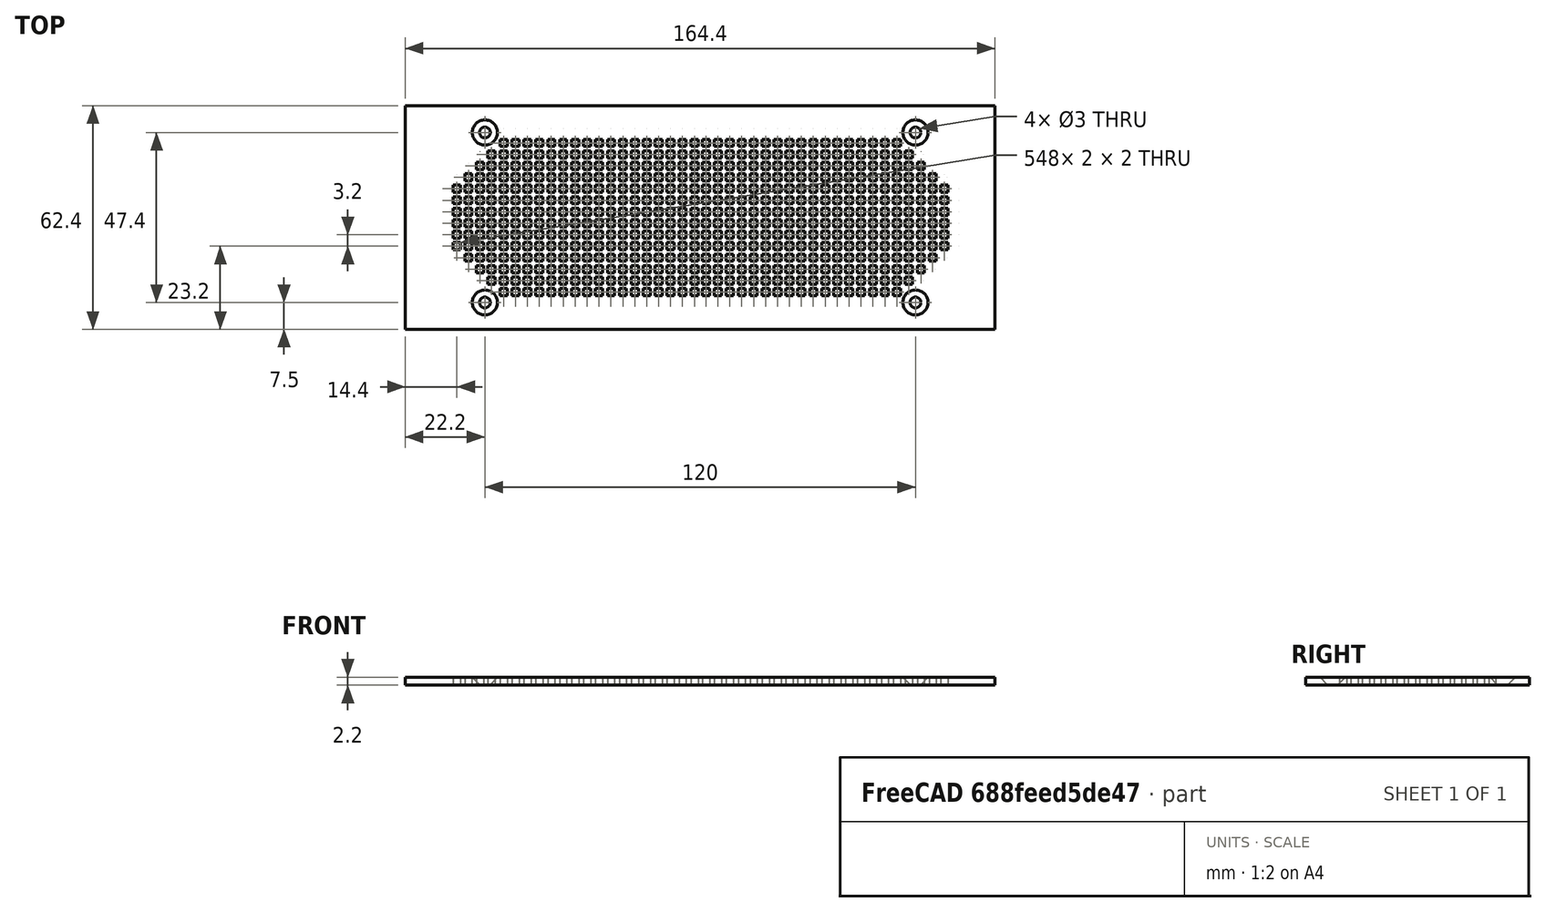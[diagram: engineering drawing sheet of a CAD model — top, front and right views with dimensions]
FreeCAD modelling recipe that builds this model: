
FCSTD DOCUMENT  (FreeCAD 0.19R24276 (Git))
Label: SpeakerCover
License: All rights reserved
LicenseURL: http://en.wikipedia.org/wiki/All_rights_reserved
objects: Sketcher::SketchObject×9, PartDesign::Pocket×8, PartDesign::LinearPattern×7, PartDesign::Pad×1, PartDesign::Chamfer×1, PartDesign::Body×1
note: 37 computed .brp shape members not serialized (recipe doc carries the construction recipe); baked Part::Feature solids carry a one-line shape summary decoded from their .brp

FEATURE [Sketcher::SketchObject] Sketch
  FullyConstrained = true
  MapMode = 5
  Support = -> [XY_Plane]
  sketch-geometry (4):
    g0: LineSegment StartX=-82.2 StartY=31.2 StartZ=0 EndX=82.2 EndY=31.2 EndZ=0
    g1: LineSegment StartX=82.2 StartY=31.2 StartZ=0 EndX=82.2 EndY=-31.2 EndZ=0
    g2: LineSegment StartX=82.2 StartY=-31.2 StartZ=0 EndX=-82.2 EndY=-31.2 EndZ=0
    g3: LineSegment StartX=-82.2 StartY=-31.2 StartZ=0 EndX=-82.2 EndY=31.2 EndZ=0
  constraints (11):
    c: Coincident(g0,g1)
    c: Coincident(g1,g2)
    c: Coincident(g2,g3)
    c: Coincident(g3,g0)
    c: Horizontal(g0)
    c: Horizontal(g2)
    c: Vertical(g1)
    c: Vertical(g3)
    c: Distance(g0) = 164.4
    c: Distance(g3) = 62.4
    c: Symmetric(g0,g1,g-1)
FEATURE [PartDesign::Pad] Pad
  Direction = (1,1,1)
  Length = 2.2
  Length2 = 100
  Profile = -> Sketch
  Type = 0
FEATURE [Sketcher::SketchObject] Sketch001
  FullyConstrained = true
  MapMode = 5
  Placement = pos=(0,0,2.2) rot=(0,0,1;0rad)
  Support = -> [Pad]
  sketch-geometry (4):
    g0: Circle CenterX=-60 CenterY=23.7 CenterZ=0 NormalX=0 NormalY=0 NormalZ=1 AngleXU=0 Radius=1.5
    g1: Circle CenterX=60 CenterY=23.7 CenterZ=0 NormalX=0 NormalY=0 NormalZ=1 AngleXU=0 Radius=1.5
    g2: Circle CenterX=-60 CenterY=-23.7 CenterZ=0 NormalX=0 NormalY=0 NormalZ=1 AngleXU=0 Radius=1.5
    g3: Circle CenterX=60 CenterY=-23.7 CenterZ=0 NormalX=0 NormalY=0 NormalZ=1 AngleXU=0 Radius=1.5
  constraints (12):
    c: DistanceX(g0,g1) = 120
    c: DistanceX(g2,g3) = 120
    c: DistanceY(g2,g0) = 47.4
    c: DistanceY(g3,g1) = 47.4
    c: DistanceY(g-1,g0) = 23.7
    c: DistanceY(g3,g-1) = 23.7
    c: DistanceX(g2,g-1) = 60
    c: DistanceX(g0,g-1) = 60
    c: Radius(g0) = 1.5
    c: Radius(g2) = 1.5
    c: Radius(g3) = 1.5
    c: Radius(g1) = 1.5
FEATURE [PartDesign::Pocket] Pocket
  BaseFeature = -> Pad
  Length = 2.2
  Length2 = 100
  Profile = -> Sketch001
  Type = 0
FEATURE [Sketcher::SketchObject] Sketch002
  FullyConstrained = true
  MapMode = 5
  Placement = pos=(0,0,2.2) rot=(0,0,1;0rad)
  Support = -> [Pocket]
  sketch-geometry (28):
    g0: LineSegment StartX=-2.6 StartY=2.6 StartZ=0 EndX=-0.6 EndY=2.6 EndZ=0
    g1: LineSegment StartX=-0.6 StartY=2.6 StartZ=0 EndX=-0.6 EndY=0.6 EndZ=0
    g2: LineSegment StartX=-0.6 StartY=0.6 StartZ=0 EndX=-2.6 EndY=0.6 EndZ=0
    g3: LineSegment StartX=-2.6 StartY=0.6 StartZ=0 EndX=-2.6 EndY=2.6 EndZ=0
    g4: LineSegment StartX=-2.6 StartY=5.8 StartZ=0 EndX=-0.6 EndY=5.8 EndZ=0
    g5: LineSegment StartX=-0.6 StartY=5.8 StartZ=0 EndX=-0.6 EndY=3.8 EndZ=0
    g6: LineSegment StartX=-0.6 StartY=3.8 StartZ=0 EndX=-2.6 EndY=3.8 EndZ=0
    g7: LineSegment StartX=-2.6 StartY=3.8 StartZ=0 EndX=-2.6 EndY=5.8 EndZ=0
    g8: LineSegment StartX=-2.6 StartY=9 StartZ=0 EndX=-0.6 EndY=9 EndZ=0
    g9: LineSegment StartX=-0.6 StartY=9 StartZ=0 EndX=-0.6 EndY=7 EndZ=0
    g10: LineSegment StartX=-0.6 StartY=7 StartZ=0 EndX=-2.6 EndY=7 EndZ=0
    g11: LineSegment StartX=-2.6 StartY=7 StartZ=0 EndX=-2.6 EndY=9 EndZ=0
    g12: LineSegment StartX=-2.6 StartY=12.2 StartZ=0 EndX=-0.6 EndY=12.2 EndZ=0
    g13: LineSegment StartX=-0.6 StartY=12.2 StartZ=0 EndX=-0.6 EndY=10.2 EndZ=0
    g14: LineSegment StartX=-0.6 StartY=10.2 StartZ=0 EndX=-2.6 EndY=10.2 EndZ=0
    g15: LineSegment StartX=-2.6 StartY=10.2 StartZ=0 EndX=-2.6 EndY=12.2 EndZ=0
    g16: LineSegment StartX=-2.6 StartY=15.4 StartZ=0 EndX=-0.6 EndY=15.4 EndZ=0
    g17: LineSegment StartX=-0.6 StartY=15.4 StartZ=0 EndX=-0.6 EndY=13.4 EndZ=0
    g18: LineSegment StartX=-0.6 StartY=13.4 StartZ=0 EndX=-2.6 EndY=13.4 EndZ=0
    g19: LineSegment StartX=-2.6 StartY=13.4 StartZ=0 EndX=-2.6 EndY=15.4 EndZ=0
    g20: LineSegment StartX=-2.6 StartY=18.6 StartZ=0 EndX=-0.6 EndY=18.6 EndZ=0
    g21: LineSegment StartX=-0.6 StartY=18.6 StartZ=0 EndX=-0.6 EndY=16.6 EndZ=0
    g22: LineSegment StartX=-0.6 StartY=16.6 StartZ=0 EndX=-2.6 EndY=16.6 EndZ=0
    g23: LineSegment StartX=-2.6 StartY=16.6 StartZ=0 EndX=-2.6 EndY=18.6 EndZ=0
    g24: LineSegment StartX=-2.6 StartY=21.8 StartZ=0 EndX=-0.6 EndY=21.8 EndZ=0
    g25: LineSegment StartX=-0.6 StartY=21.8 StartZ=0 EndX=-0.6 EndY=19.8 EndZ=0
    g26: LineSegment StartX=-0.6 StartY=19.8 StartZ=0 EndX=-2.6 EndY=19.8 EndZ=0
    g27: LineSegment StartX=-2.6 StartY=19.8 StartZ=0 EndX=-2.6 EndY=21.8 EndZ=0
  constraints (84):
    c: Coincident(g0,g1)
    c: Coincident(g1,g2)
    c: Coincident(g2,g3)
    c: Coincident(g3,g0)
    c: Horizontal(g0)
    c: Horizontal(g2)
    c: Vertical(g1)
    c: Vertical(g3)
    c: Distance(g0) = 2
    c: Distance(g1) = 2
    c: DistanceX(g1,g-1) = 0.6
    c: DistanceY(g-1,g1) = 0.6
    c: Coincident(g4,g5)
    c: Coincident(g5,g6)
    c: Coincident(g6,g7)
    c: Coincident(g7,g4)
    c: Horizontal(g4)
    c: Horizontal(g6)
    c: Vertical(g5)
    c: Vertical(g7)
    c: Distance(g4) = 2
    c: Distance(g5) = 2
    c: DistanceX(g5,g-1) = 0.6
    c: DistanceY(g0,g5) = 1.2
    c: Coincident(g8,g9)
    c: Coincident(g9,g10)
    c: Coincident(g10,g11)
    c: Coincident(g11,g8)
    c: Horizontal(g8)
    c: Horizontal(g10)
    c: Vertical(g9)
    c: Vertical(g11)
    c: Distance(g8) = 2
    c: Distance(g9) = 2
    c: DistanceX(g9,g-1) = 0.6
    c: DistanceY(g4,g9) = 1.2
    c: Coincident(g12,g13)
    c: Coincident(g13,g14)
    c: Coincident(g14,g15)
    c: Coincident(g15,g12)
    c: Horizontal(g12)
    c: Horizontal(g14)
    c: Vertical(g13)
    c: Vertical(g15)
    c: Distance(g12) = 2
    c: Distance(g13) = 2
    c: DistanceX(g13,g-1) = 0.6
    c: DistanceY(g8,g13) = 1.2
    c: Coincident(g16,g17)
    c: Coincident(g17,g18)
    c: Coincident(g18,g19)
    c: Coincident(g19,g16)
    c: Horizontal(g16)
    c: Horizontal(g18)
    c: Vertical(g17)
    c: Vertical(g19)
    c: Distance(g16) = 2
    c: Distance(g17) = 2
    c: DistanceX(g17,g-1) = 0.6
    c: DistanceY(g12,g17) = 1.2
    c: Coincident(g20,g21)
    c: Coincident(g21,g22)
    c: Coincident(g22,g23)
    c: Coincident(g23,g20)
    c: Horizontal(g20)
    c: Horizontal(g22)
    c: Vertical(g21)
    c: Vertical(g23)
    c: Distance(g20) = 2
    c: Distance(g21) = 2
    c: DistanceY(g16,g21) = 1.2
    c: DistanceX(g21,g-1) = 0.6
    c: Coincident(g24,g25)
    c: Coincident(g25,g26)
    c: Coincident(g26,g27)
    c: Coincident(g27,g24)
    c: Horizontal(g24)
    c: Horizontal(g26)
    c: Vertical(g25)
    c: Vertical(g27)
    c: Distance(g24) = 2
    c: Distance(g25) = 2
    c: DistanceX(g25,g-1) = 0.6
    c: DistanceY(g20,g25) = 1.2
FEATURE [PartDesign::Pocket] Pocket001
  BaseFeature = -> Pocket
  Length = 2.2
  Length2 = 100
  Profile = -> Sketch002
  Type = 0
FEATURE [PartDesign::LinearPattern] LinearPattern
  BaseFeature = -> Pocket001
  Direction = -> Sketch002 [H_Axis]
  Length = 53.2
  Occurrences = 17
  Originals = -> [Pocket001]
  Reversed = true
FEATURE [Sketcher::SketchObject] Sketch003
  FullyConstrained = true
  MapMode = 5
  Placement = pos=(0,0,2.2) rot=(0,0,1;0rad)
  Support = -> [LinearPattern]
  sketch-geometry (28):
    g0: LineSegment StartX=-2.6 StartY=-0.6 StartZ=0 EndX=-0.6 EndY=-0.6 EndZ=0
    g1: LineSegment StartX=-0.6 StartY=-0.6 StartZ=0 EndX=-0.6 EndY=-2.6 EndZ=0
    g2: LineSegment StartX=-0.6 StartY=-2.6 StartZ=0 EndX=-2.6 EndY=-2.6 EndZ=0
    g3: LineSegment StartX=-2.6 StartY=-2.6 StartZ=0 EndX=-2.6 EndY=-0.6 EndZ=0
    g4: LineSegment StartX=-2.6 StartY=-3.8 StartZ=0 EndX=-0.6 EndY=-3.8 EndZ=0
    g5: LineSegment StartX=-0.6 StartY=-3.8 StartZ=0 EndX=-0.6 EndY=-5.8 EndZ=0
    g6: LineSegment StartX=-0.6 StartY=-5.8 StartZ=0 EndX=-2.6 EndY=-5.8 EndZ=0
    g7: LineSegment StartX=-2.6 StartY=-5.8 StartZ=0 EndX=-2.6 EndY=-3.8 EndZ=0
    g8: LineSegment StartX=-2.6 StartY=-7 StartZ=0 EndX=-0.6 EndY=-7 EndZ=0
    g9: LineSegment StartX=-0.6 StartY=-7 StartZ=0 EndX=-0.6 EndY=-9 EndZ=0
    g10: LineSegment StartX=-0.6 StartY=-9 StartZ=0 EndX=-2.6 EndY=-9 EndZ=0
    g11: LineSegment StartX=-2.6 StartY=-9 StartZ=0 EndX=-2.6 EndY=-7 EndZ=0
    g12: LineSegment StartX=-2.6 StartY=-10.2 StartZ=0 EndX=-0.6 EndY=-10.2 EndZ=0
    g13: LineSegment StartX=-0.6 StartY=-10.2 StartZ=0 EndX=-0.6 EndY=-12.2 EndZ=0
    g14: LineSegment StartX=-0.6 StartY=-12.2 StartZ=0 EndX=-2.6 EndY=-12.2 EndZ=0
    g15: LineSegment StartX=-2.6 StartY=-12.2 StartZ=0 EndX=-2.6 EndY=-10.2 EndZ=0
    g16: LineSegment StartX=-2.6 StartY=-13.4 StartZ=0 EndX=-0.6 EndY=-13.4 EndZ=0
    g17: LineSegment StartX=-0.6 StartY=-13.4 StartZ=0 EndX=-0.6 EndY=-15.4 EndZ=0
    g18: LineSegment StartX=-0.6 StartY=-15.4 StartZ=0 EndX=-2.6 EndY=-15.4 EndZ=0
    g19: LineSegment StartX=-2.6 StartY=-15.4 StartZ=0 EndX=-2.6 EndY=-13.4 EndZ=0
    g20: LineSegment StartX=-2.6 StartY=-16.6 StartZ=0 EndX=-0.6 EndY=-16.6 EndZ=0
    g21: LineSegment StartX=-0.6 StartY=-16.6 StartZ=0 EndX=-0.6 EndY=-18.6 EndZ=0
    g22: LineSegment StartX=-0.6 StartY=-18.6 StartZ=0 EndX=-2.6 EndY=-18.6 EndZ=0
    g23: LineSegment StartX=-2.6 StartY=-18.6 StartZ=0 EndX=-2.6 EndY=-16.6 EndZ=0
    g24: LineSegment StartX=-2.6 StartY=-19.8 StartZ=0 EndX=-0.6 EndY=-19.8 EndZ=0
    g25: LineSegment StartX=-0.6 StartY=-19.8 StartZ=0 EndX=-0.6 EndY=-21.8 EndZ=0
    g26: LineSegment StartX=-0.6 StartY=-21.8 StartZ=0 EndX=-2.6 EndY=-21.8 EndZ=0
    g27: LineSegment StartX=-2.6 StartY=-21.8 StartZ=0 EndX=-2.6 EndY=-19.8 EndZ=0
  constraints (84):
    c: Coincident(g0,g1)
    c: Coincident(g1,g2)
    c: Coincident(g2,g3)
    c: Coincident(g3,g0)
    c: Horizontal(g0)
    c: Horizontal(g2)
    c: Vertical(g1)
    c: Vertical(g3)
    c: Coincident(g4,g5)
    c: Coincident(g5,g6)
    c: Coincident(g6,g7)
    c: Coincident(g7,g4)
    c: Horizontal(g4)
    c: Horizontal(g6)
    c: Vertical(g5)
    c: Vertical(g7)
    c: Coincident(g8,g9)
    c: Coincident(g9,g10)
    c: Coincident(g10,g11)
    c: Coincident(g11,g8)
    c: Horizontal(g8)
    c: Horizontal(g10)
    c: Vertical(g9)
    c: Vertical(g11)
    c: Coincident(g12,g13)
    c: Coincident(g13,g14)
    c: Coincident(g14,g15)
    c: Coincident(g15,g12)
    c: Horizontal(g12)
    c: Horizontal(g14)
    c: Vertical(g13)
    c: Vertical(g15)
    c: Coincident(g16,g17)
    c: Coincident(g17,g18)
    c: Coincident(g18,g19)
    c: Coincident(g19,g16)
    c: Horizontal(g16)
    c: Horizontal(g18)
    c: Vertical(g17)
    c: Vertical(g19)
    c: Coincident(g20,g21)
    c: Coincident(g21,g22)
    c: Coincident(g22,g23)
    c: Coincident(g23,g20)
    c: Horizontal(g20)
    c: Horizontal(g22)
    c: Vertical(g21)
    c: Vertical(g23)
    c: Coincident(g24,g25)
    c: Coincident(g25,g26)
    c: Coincident(g26,g27)
    c: Coincident(g27,g24)
    c: Horizontal(g24)
    c: Horizontal(g26)
    c: Vertical(g25)
    c: Vertical(g27)
    c: Distance(g0) = 2
    c: Distance(g1) = 2
    c: Distance(g4) = 2
    c: Distance(g5) = 2
    c: Distance(g8) = 2
    c: Distance(g9) = 2
    c: Distance(g12) = 2
    c: Distance(g13) = 2
    c: Distance(g16) = 2
    c: Distance(g17) = 2
    c: Distance(g20) = 2
    c: Distance(g21) = 2
    c: Distance(g24) = 2
    c: Distance(g25) = 2
    c: DistanceY(g0,g-1) = 0.6
    c: DistanceY(g4,g1) = 1.2
    c: DistanceY(g8,g5) = 1.2
    c: DistanceX(g0,g-1) = 0.6
    c: DistanceX(g4,g-1) = 0.6
    c: DistanceX(g8,g-1) = 0.6
    c: DistanceX(g12,g-1) = 0.6
    c: DistanceX(g16,g-1) = 0.6
    c: DistanceX(g20,g-1) = 0.6
    c: DistanceX(g24,g-1) = 0.6
    c: DistanceY(g12,g9) = 1.2
    c: DistanceY(g16,g13) = 1.2
    c: DistanceY(g20,g17) = 1.2
    c: DistanceY(g24,g21) = 1.2
FEATURE [PartDesign::Pocket] Pocket002
  BaseFeature = -> LinearPattern
  Length = 2.2
  Length2 = 100
  Profile = -> Sketch003
  Type = 0
FEATURE [PartDesign::LinearPattern] LinearPattern001
  BaseFeature = -> Pocket002
  Direction = -> Sketch003 [H_Axis]
  Length = 53.2
  Occurrences = 17
  Originals = -> [Pocket002]
  Reversed = true
FEATURE [Sketcher::SketchObject] Sketch004
  FullyConstrained = true
  MapMode = 5
  Placement = pos=(0,0,2.2) rot=(0,0,1;0rad)
  Support = -> [LinearPattern001]
  sketch-geometry (56):
    g0: LineSegment StartX=0.6 StartY=2.6 StartZ=0 EndX=2.6 EndY=2.6 EndZ=0
    g1: LineSegment StartX=2.6 StartY=2.6 StartZ=0 EndX=2.6 EndY=0.6 EndZ=0
    g2: LineSegment StartX=2.6 StartY=0.6 StartZ=0 EndX=0.6 EndY=0.6 EndZ=0
    g3: LineSegment StartX=0.6 StartY=0.6 StartZ=0 EndX=0.6 EndY=2.6 EndZ=0
    g4: LineSegment StartX=0.6 StartY=5.8 StartZ=0 EndX=2.6 EndY=5.8 EndZ=0
    g5: LineSegment StartX=2.6 StartY=5.8 StartZ=0 EndX=2.6 EndY=3.8 EndZ=0
    g6: LineSegment StartX=2.6 StartY=3.8 StartZ=0 EndX=0.6 EndY=3.8 EndZ=0
    g7: LineSegment StartX=0.6 StartY=3.8 StartZ=0 EndX=0.6 EndY=5.8 EndZ=0
    g8: LineSegment StartX=0.6 StartY=9 StartZ=0 EndX=2.6 EndY=9 EndZ=0
    g9: LineSegment StartX=2.6 StartY=9 StartZ=0 EndX=2.6 EndY=7 EndZ=0
    g10: LineSegment StartX=2.6 StartY=7 StartZ=0 EndX=0.6 EndY=7 EndZ=0
    g11: LineSegment StartX=0.6 StartY=7 StartZ=0 EndX=0.6 EndY=9 EndZ=0
    g12: LineSegment StartX=0.6 StartY=12.2 StartZ=0 EndX=2.6 EndY=12.2 EndZ=0
    g13: LineSegment StartX=2.6 StartY=12.2 StartZ=0 EndX=2.6 EndY=10.2 EndZ=0
    g14: LineSegment StartX=2.6 StartY=10.2 StartZ=0 EndX=0.6 EndY=10.2 EndZ=0
    g15: LineSegment StartX=0.6 StartY=10.2 StartZ=0 EndX=0.6 EndY=12.2 EndZ=0
    g16: LineSegment StartX=0.6 StartY=15.4 StartZ=0 EndX=2.6 EndY=15.4 EndZ=0
    g17: LineSegment StartX=2.6 StartY=15.4 StartZ=0 EndX=2.6 EndY=13.4 EndZ=0
    g18: LineSegment StartX=2.6 StartY=13.4 StartZ=0 EndX=0.6 EndY=13.4 EndZ=0
    g19: LineSegment StartX=0.6 StartY=13.4 StartZ=0 EndX=0.6 EndY=15.4 EndZ=0
    g20: LineSegment StartX=0.6 StartY=21.8 StartZ=0 EndX=2.6 EndY=21.8 EndZ=0
    g21: LineSegment StartX=2.6 StartY=21.8 StartZ=0 EndX=2.6 EndY=19.8 EndZ=0
    g22: LineSegment StartX=2.6 StartY=19.8 StartZ=0 EndX=0.6 EndY=19.8 EndZ=0
    g23: LineSegment StartX=0.6 StartY=19.8 StartZ=0 EndX=0.6 EndY=21.8 EndZ=0
    g24: LineSegment StartX=0.6 StartY=18.6 StartZ=0 EndX=2.6 EndY=18.6 EndZ=0
    g25: LineSegment StartX=2.6 StartY=18.6 StartZ=0 EndX=2.6 EndY=16.6 EndZ=0
    g26: LineSegment StartX=2.6 StartY=16.6 StartZ=0 EndX=0.6 EndY=16.6 EndZ=0
    g27: LineSegment StartX=0.6 StartY=16.6 StartZ=0 EndX=0.6 EndY=18.6 EndZ=0
    g28: LineSegment StartX=0.6 StartY=-0.6 StartZ=0 EndX=2.6 EndY=-0.6 EndZ=0
    g29: LineSegment StartX=2.6 StartY=-0.6 StartZ=0 EndX=2.6 EndY=-2.6 EndZ=0
    g30: LineSegment StartX=2.6 StartY=-2.6 StartZ=0 EndX=0.6 EndY=-2.6 EndZ=0
    g31: LineSegment StartX=0.6 StartY=-2.6 StartZ=0 EndX=0.6 EndY=-0.6 EndZ=0
    g32: LineSegment StartX=0.6 StartY=-3.8 StartZ=0 EndX=2.6 EndY=-3.8 EndZ=0
    g33: LineSegment StartX=2.6 StartY=-3.8 StartZ=0 EndX=2.6 EndY=-5.8 EndZ=0
    g34: LineSegment StartX=2.6 StartY=-5.8 StartZ=0 EndX=0.6 EndY=-5.8 EndZ=0
    g35: LineSegment StartX=0.6 StartY=-5.8 StartZ=0 EndX=0.6 EndY=-3.8 EndZ=0
    g36: LineSegment StartX=0.6 StartY=-10.2 StartZ=0 EndX=2.6 EndY=-10.2 EndZ=0
    g37: LineSegment StartX=2.6 StartY=-10.2 StartZ=0 EndX=2.6 EndY=-12.2 EndZ=0
    g38: LineSegment StartX=2.6 StartY=-12.2 StartZ=0 EndX=0.6 EndY=-12.2 EndZ=0
    g39: LineSegment StartX=0.6 StartY=-12.2 StartZ=0 EndX=0.6 EndY=-10.2 EndZ=0
    g40: LineSegment StartX=0.6 StartY=-16.6 StartZ=0 EndX=2.6 EndY=-16.6 EndZ=0
    g41: LineSegment StartX=2.6 StartY=-16.6 StartZ=0 EndX=2.6 EndY=-18.6 EndZ=0
    g42: LineSegment StartX=2.6 StartY=-18.6 StartZ=0 EndX=0.6 EndY=-18.6 EndZ=0
    g43: LineSegment StartX=0.6 StartY=-18.6 StartZ=0 EndX=0.6 EndY=-16.6 EndZ=0
    g44: LineSegment StartX=0.6 StartY=-13.4 StartZ=0 EndX=2.6 EndY=-13.4 EndZ=0
    g45: LineSegment StartX=2.6 StartY=-13.4 StartZ=0 EndX=2.6 EndY=-15.4 EndZ=0
    g46: LineSegment StartX=2.6 StartY=-15.4 StartZ=0 EndX=0.6 EndY=-15.4 EndZ=0
    g47: LineSegment StartX=0.6 StartY=-15.4 StartZ=0 EndX=0.6 EndY=-13.4 EndZ=0
    g48: LineSegment StartX=0.6 StartY=-19.8 StartZ=0 EndX=2.6 EndY=-19.8 EndZ=0
    g49: LineSegment StartX=2.6 StartY=-19.8 StartZ=0 EndX=2.6 EndY=-21.8 EndZ=0
    g50: LineSegment StartX=2.6 StartY=-21.8 StartZ=0 EndX=0.6 EndY=-21.8 EndZ=0
    g51: LineSegment StartX=0.6 StartY=-21.8 StartZ=0 EndX=0.6 EndY=-19.8 EndZ=0
    g52: LineSegment StartX=0.6 StartY=-7 StartZ=0 EndX=2.6 EndY=-7 EndZ=0
    g53: LineSegment StartX=2.6 StartY=-7 StartZ=0 EndX=2.6 EndY=-9 EndZ=0
    g54: LineSegment StartX=2.6 StartY=-9 StartZ=0 EndX=0.6 EndY=-9 EndZ=0
    g55: LineSegment StartX=0.6 StartY=-9 StartZ=0 EndX=0.6 EndY=-7 EndZ=0
  constraints (168):
    c: Coincident(g0,g1)
    c: Coincident(g1,g2)
    c: Coincident(g2,g3)
    c: Coincident(g3,g0)
    c: Horizontal(g0)
    c: Horizontal(g2)
    c: Vertical(g1)
    c: Vertical(g3)
    c: Coincident(g4,g5)
    c: Coincident(g5,g6)
    c: Coincident(g6,g7)
    c: Coincident(g7,g4)
    c: Horizontal(g4)
    c: Horizontal(g6)
    c: Vertical(g5)
    c: Vertical(g7)
    c: Coincident(g8,g9)
    c: Coincident(g9,g10)
    c: Coincident(g10,g11)
    c: Coincident(g11,g8)
    c: Horizontal(g8)
    c: Horizontal(g10)
    c: Vertical(g9)
    c: Vertical(g11)
    c: Coincident(g12,g13)
    c: Coincident(g13,g14)
    c: Coincident(g14,g15)
    c: Coincident(g15,g12)
    c: Horizontal(g12)
    c: Horizontal(g14)
    c: Vertical(g13)
    c: Vertical(g15)
    c: Coincident(g16,g17)
    c: Coincident(g17,g18)
    c: Coincident(g18,g19)
    c: Coincident(g19,g16)
    c: Horizontal(g16)
    c: Horizontal(g18)
    c: Vertical(g17)
    c: Vertical(g19)
    c: Coincident(g20,g21)
    c: Coincident(g21,g22)
    c: Coincident(g22,g23)
    c: Coincident(g23,g20)
    c: Horizontal(g20)
    c: Horizontal(g22)
    c: Vertical(g21)
    c: Vertical(g23)
    c: Coincident(g24,g25)
    c: Coincident(g25,g26)
    c: Coincident(g26,g27)
    c: Coincident(g27,g24)
    c: Horizontal(g24)
    c: Horizontal(g26)
    c: Vertical(g25)
    c: Vertical(g27)
    c: Distance(g0) = 2
    c: Distance(g1) = 2
    c: Distance(g4) = 2
    c: Distance(g5) = 2
    c: Distance(g8) = 2
    c: Distance(g9) = 2
    c: Distance(g12) = 2
    c: Distance(g13) = 2
    c: Distance(g16) = 2
    c: Distance(g17) = 2
    c: Distance(g20) = 2
    c: Distance(g23) = 2
    c: Distance(g25) = 2
    c: Distance(g24) = 2
    c: DistanceY(g-1,g2) = 0.6
    c: DistanceY(g0,g6) = 1.2
    c: DistanceY(g4,g10) = 1.2
    c: DistanceY(g8,g14) = 1.2
    c: DistanceX(g-1,g2) = 0.6
    c: DistanceX(g-1,g6) = 0.6
    c: DistanceX(g-1,g10) = 0.6
    c: DistanceX(g-1,g14) = 0.6
    c: DistanceX(g-1,g18) = 0.6
    c: DistanceY(g12,g18) = 1.2
    c: DistanceY(g16,g26) = 1.2
    c: DistanceY(g24,g22) = 1.2
    c: DistanceX(g-1,g26) = 0.6
    c: DistanceX(g-1,g22) = 0.6
    c: Coincident(g28,g29)
    c: Coincident(g29,g30)
    c: Coincident(g30,g31)
    c: Coincident(g31,g28)
    c: Horizontal(g28)
    c: Horizontal(g30)
    c: Vertical(g29)
    c: Vertical(g31)
    c: Coincident(g32,g33)
    c: Coincident(g33,g34)
    c: Coincident(g34,g35)
    c: Coincident(g35,g32)
    c: Horizontal(g32)
    c: Horizontal(g34)
    c: Vertical(g33)
    c: Vertical(g35)
    c: Coincident(g36,g37)
    c: Coincident(g37,g38)
    c: Coincident(g38,g39)
    c: Coincident(g39,g36)
    c: Horizontal(g36)
    c: Horizontal(g38)
    c: Vertical(g37)
    c: Vertical(g39)
    c: Coincident(g40,g41)
    c: Coincident(g41,g42)
    c: Coincident(g42,g43)
    c: Coincident(g43,g40)
    c: Horizontal(g40)
    c: Horizontal(g42)
    c: Vertical(g41)
    c: Vertical(g43)
    c: Coincident(g44,g45)
    c: Coincident(g45,g46)
    c: Coincident(g46,g47)
    c: Coincident(g47,g44)
    c: Horizontal(g44)
    c: Horizontal(g46)
    c: Vertical(g45)
    c: Vertical(g47)
    c: Coincident(g48,g49)
    c: Coincident(g49,g50)
    c: Coincident(g50,g51)
    c: Coincident(g51,g48)
    c: Horizontal(g48)
    c: Horizontal(g50)
    c: Vertical(g49)
    c: Vertical(g51)
    c: Coincident(g52,g53)
    c: Coincident(g53,g54)
    c: Coincident(g54,g55)
    c: Coincident(g55,g52)
    c: Horizontal(g52)
    c: Horizontal(g54)
    c: Vertical(g53)
    c: Vertical(g55)
    c: Distance(g28) = 2
    c: Distance(g29) = 2
    c: Distance(g32) = 2
    c: Distance(g33) = 2
    c: Distance(g52) = 2
    c: Distance(g53) = 2
    c: DistanceY(g28,g-1) = 0.6
    c: DistanceY(g32,g30) = 1.2
    c: DistanceY(g52,g34) = 1.2
    c: DistanceX(g-1,g28) = 0.6
    c: DistanceX(g-1,g32) = 0.6
    c: DistanceX(g-1,g52) = 0.6
    c: Distance(g36) = 2
    c: Distance(g37) = 2
    c: Distance(g46) = 2
    c: Distance(g45) = 2
    c: DistanceX(g-1,g36) = 0.6
    c: DistanceX(g-1,g44) = 0.6
    c: DistanceY(g36,g54) = 1.2
    c: DistanceY(g44,g38) = 1.2
    c: Distance(g40) = 2
    c: Distance(g41) = 2
    c: Distance(g51) = 2
    c: Distance(g48) = 2
    c: DistanceY(g40,g46) = 1.2
    c: DistanceY(g48,g42) = 1.2
    c: DistanceX(g-1,g40) = 0.6
    c: DistanceX(g-1,g48) = 0.6
FEATURE [PartDesign::Pocket] Pocket003
  BaseFeature = -> LinearPattern001
  Length = 2.2
  Length2 = 100
  Profile = -> Sketch004
  Type = 0
FEATURE [PartDesign::LinearPattern] LinearPattern002
  BaseFeature = -> Pocket003
  Direction = -> Sketch004 [H_Axis]
  Length = 53.2
  Occurrences = 17
  Originals = -> [Pocket003]
FEATURE [Sketcher::SketchObject] Sketch005
  FullyConstrained = true
  MapMode = 5
  Placement = pos=(0,0,2.2) rot=(0,0,1;0rad)
  Support = -> [LinearPattern002]
  sketch-geometry (48):
    g0: LineSegment StartX=-59.2 StartY=2.6 StartZ=0 EndX=-57.2 EndY=2.6 EndZ=0
    g1: LineSegment StartX=-57.2 StartY=2.6 StartZ=0 EndX=-57.2 EndY=0.6 EndZ=0
    g2: LineSegment StartX=-57.2 StartY=0.6 StartZ=0 EndX=-59.2 EndY=0.6 EndZ=0
    g3: LineSegment StartX=-59.2 StartY=0.6 StartZ=0 EndX=-59.2 EndY=2.6 EndZ=0
    g4: LineSegment StartX=-59.2 StartY=-0.6 StartZ=0 EndX=-57.2 EndY=-0.6 EndZ=0
    g5: LineSegment StartX=-57.2 StartY=-0.6 StartZ=0 EndX=-57.2 EndY=-2.6 EndZ=0
    g6: LineSegment StartX=-57.2 StartY=-2.6 StartZ=0 EndX=-59.2 EndY=-2.6 EndZ=0
    g7: LineSegment StartX=-59.2 StartY=-2.6 StartZ=0 EndX=-59.2 EndY=-0.6 EndZ=0
    g8: LineSegment StartX=-59.2 StartY=5.8 StartZ=0 EndX=-57.2 EndY=5.8 EndZ=0
    g9: LineSegment StartX=-57.2 StartY=5.8 StartZ=0 EndX=-57.2 EndY=3.8 EndZ=0
    g10: LineSegment StartX=-57.2 StartY=3.8 StartZ=0 EndX=-59.2 EndY=3.8 EndZ=0
    g11: LineSegment StartX=-59.2 StartY=3.8 StartZ=0 EndX=-59.2 EndY=5.8 EndZ=0
    g12: LineSegment StartX=-59.2 StartY=9 StartZ=0 EndX=-57.2 EndY=9 EndZ=0
    g13: LineSegment StartX=-57.2 StartY=9 StartZ=0 EndX=-57.2 EndY=7 EndZ=0
    g14: LineSegment StartX=-57.2 StartY=7 StartZ=0 EndX=-59.2 EndY=7 EndZ=0
    g15: LineSegment StartX=-59.2 StartY=7 StartZ=0 EndX=-59.2 EndY=9 EndZ=0
    g16: LineSegment StartX=-59.2 StartY=12.2 StartZ=0 EndX=-57.2 EndY=12.2 EndZ=0
    g17: LineSegment StartX=-57.2 StartY=12.2 StartZ=0 EndX=-57.2 EndY=10.2 EndZ=0
    g18: LineSegment StartX=-57.2 StartY=10.2 StartZ=0 EndX=-59.2 EndY=10.2 EndZ=0
    g19: LineSegment StartX=-59.2 StartY=10.2 StartZ=0 EndX=-59.2 EndY=12.2 EndZ=0
    g20: LineSegment StartX=-59.2 StartY=15.4 StartZ=0 EndX=-57.2 EndY=15.4 EndZ=0
    g21: LineSegment StartX=-57.2 StartY=15.4 StartZ=0 EndX=-57.2 EndY=13.4 EndZ=0
    g22: LineSegment StartX=-57.2 StartY=13.4 StartZ=0 EndX=-59.2 EndY=13.4 EndZ=0
    g23: LineSegment StartX=-59.2 StartY=13.4 StartZ=0 EndX=-59.2 EndY=15.4 EndZ=0
    g24: LineSegment StartX=-57.2 StartY=18.6 StartZ=0 EndX=-59.2 EndY=18.6 EndZ=0
    g25: LineSegment StartX=-59.2 StartY=18.6 StartZ=0 EndX=-59.2 EndY=16.6 EndZ=0
    g26: LineSegment StartX=-59.2 StartY=16.6 StartZ=0 EndX=-57.2 EndY=16.6 EndZ=0
    g27: LineSegment StartX=-57.2 StartY=16.6 StartZ=0 EndX=-57.2 EndY=18.6 EndZ=0
    g28: LineSegment StartX=-57.2 StartY=-3.8 StartZ=0 EndX=-59.2 EndY=-3.8 EndZ=0
    g29: LineSegment StartX=-59.2 StartY=-3.8 StartZ=0 EndX=-59.2 EndY=-5.8 EndZ=0
    g30: LineSegment StartX=-59.2 StartY=-5.8 StartZ=0 EndX=-57.2 EndY=-5.8 EndZ=0
    g31: LineSegment StartX=-57.2 StartY=-5.8 StartZ=0 EndX=-57.2 EndY=-3.8 EndZ=0
    g32: LineSegment StartX=-57.2 StartY=-7 StartZ=0 EndX=-59.2 EndY=-7 EndZ=0
    g33: LineSegment StartX=-59.2 StartY=-7 StartZ=0 EndX=-59.2 EndY=-9 EndZ=0
    g34: LineSegment StartX=-59.2 StartY=-9 StartZ=0 EndX=-57.2 EndY=-9 EndZ=0
    g35: LineSegment StartX=-57.2 StartY=-9 StartZ=0 EndX=-57.2 EndY=-7 EndZ=0
    g36: LineSegment StartX=-57.2 StartY=-10.2 StartZ=0 EndX=-59.2 EndY=-10.2 EndZ=0
    g37: LineSegment StartX=-59.2 StartY=-10.2 StartZ=0 EndX=-59.2 EndY=-12.2 EndZ=0
    g38: LineSegment StartX=-59.2 StartY=-12.2 StartZ=0 EndX=-57.2 EndY=-12.2 EndZ=0
    g39: LineSegment StartX=-57.2 StartY=-12.2 StartZ=0 EndX=-57.2 EndY=-10.2 EndZ=0
    g40: LineSegment StartX=-59.2 StartY=-13.4 StartZ=0 EndX=-57.2 EndY=-13.4 EndZ=0
    g41: LineSegment StartX=-57.2 StartY=-13.4 StartZ=0 EndX=-57.2 EndY=-15.4 EndZ=0
    g42: LineSegment StartX=-57.2 StartY=-15.4 StartZ=0 EndX=-59.2 EndY=-15.4 EndZ=0
    g43: LineSegment StartX=-59.2 StartY=-15.4 StartZ=0 EndX=-59.2 EndY=-13.4 EndZ=0
    g44: LineSegment StartX=-59.2 StartY=-16.6 StartZ=0 EndX=-57.2 EndY=-16.6 EndZ=0
    g45: LineSegment StartX=-57.2 StartY=-16.6 StartZ=0 EndX=-57.2 EndY=-18.6 EndZ=0
    g46: LineSegment StartX=-57.2 StartY=-18.6 StartZ=0 EndX=-59.2 EndY=-18.6 EndZ=0
    g47: LineSegment StartX=-59.2 StartY=-18.6 StartZ=0 EndX=-59.2 EndY=-16.6 EndZ=0
  constraints (144):
    c: Coincident(g0,g1)
    c: Coincident(g1,g2)
    c: Coincident(g2,g3)
    c: Coincident(g3,g0)
    c: Horizontal(g0)
    c: Horizontal(g2)
    c: Vertical(g1)
    c: Vertical(g3)
    c: Coincident(g4,g5)
    c: Coincident(g5,g6)
    c: Coincident(g6,g7)
    c: Coincident(g7,g4)
    c: Horizontal(g4)
    c: Horizontal(g6)
    c: Vertical(g5)
    c: Vertical(g7)
    c: Distance(g4) = 2
    c: Distance(g5) = 2
    c: Distance(g0) = 2
    c: Distance(g1) = 2
    c: DistanceY(g4,g-1) = 0.6
    c: DistanceY(g-1,g1) = 0.6
    c: DistanceX(g1,g-1) = 57.2
    c: DistanceX(g4,g-1) = 57.2
    c: Coincident(g8,g9)
    c: Coincident(g9,g10)
    c: Coincident(g10,g11)
    c: Coincident(g11,g8)
    c: Horizontal(g8)
    c: Horizontal(g10)
    c: Vertical(g9)
    c: Vertical(g11)
    c: Coincident(g12,g13)
    c: Coincident(g13,g14)
    c: Coincident(g14,g15)
    c: Coincident(g15,g12)
    c: Horizontal(g12)
    c: Horizontal(g14)
    c: Vertical(g13)
    c: Vertical(g15)
    c: Coincident(g16,g17)
    c: Coincident(g17,g18)
    c: Coincident(g18,g19)
    c: Coincident(g19,g16)
    c: Horizontal(g16)
    c: Horizontal(g18)
    c: Vertical(g17)
    c: Vertical(g19)
    c: Coincident(g20,g21)
    c: Coincident(g21,g22)
    c: Coincident(g22,g23)
    c: Coincident(g23,g20)
    c: Horizontal(g20)
    c: Horizontal(g22)
    c: Vertical(g21)
    c: Vertical(g23)
    c: Coincident(g24,g25)
    c: Coincident(g25,g26)
    c: Coincident(g26,g27)
    c: Coincident(g27,g24)
    c: Horizontal(g24)
    c: Horizontal(g26)
    c: Vertical(g25)
    c: Vertical(g27)
    c: Coincident(g28,g29)
    c: Coincident(g29,g30)
    c: Coincident(g30,g31)
    c: Coincident(g31,g28)
    c: Horizontal(g28)
    c: Horizontal(g30)
    c: Vertical(g29)
    c: Vertical(g31)
    c: Coincident(g32,g33)
    c: Coincident(g33,g34)
    c: Coincident(g34,g35)
    c: Coincident(g35,g32)
    c: Horizontal(g32)
    c: Horizontal(g34)
    c: Vertical(g33)
    c: Vertical(g35)
    c: Coincident(g36,g37)
    c: Coincident(g37,g38)
    c: Coincident(g38,g39)
    c: Coincident(g39,g36)
    c: Horizontal(g36)
    c: Horizontal(g38)
    c: Vertical(g37)
    c: Vertical(g39)
    c: Distance(g8) = 2
    c: Distance(g9) = 2
    c: Distance(g13) = 2
    c: Distance(g12) = 2
    c: Distance(g18) = 2
    c: Distance(g19) = 2
    c: Distance(g21) = 2
    c: Distance(g22) = 2
    c: DistanceY(g0,g9) = 1.2
    c: DistanceY(g8,g14) = 1.2
    c: DistanceY(g12,g18) = 1.2
    c: DistanceY(g16,g22) = 1.2
    c: DistanceX(g9,g-1) = 57.2
    c: DistanceX(g13,g-1) = 57.2
    c: DistanceX(g17,g-1) = 57.2
    c: DistanceX(g21,g-1) = 57.2
    c: Distance(g24) = 2
    c: Distance(g27) = 2
    c: DistanceY(g20,g25) = 1.2
    c: DistanceX(g26,g-1) = 57.2
    c: Distance(g28) = 2
    c: Distance(g31) = 2
    c: Distance(g32) = 2
    c: Distance(g35) = 2
    c: Distance(g36) = 2
    c: Distance(g39) = 2
    c: DistanceY(g28,g6) = 1.2
    c: DistanceY(g32,g29) = 1.2
    c: DistanceY(g36,g33) = 1.2
    c: DistanceX(g28,g-1) = 57.2
    c: DistanceX(g32,g-1) = 57.2
    c: DistanceX(g36,g-1) = 57.2
    c: Coincident(g40,g41)
    c: Coincident(g41,g42)
    c: Coincident(g42,g43)
    c: Coincident(g43,g40)
    c: Horizontal(g40)
    c: Horizontal(g42)
    c: Vertical(g41)
    c: Vertical(g43)
    c: Coincident(g44,g45)
    c: Coincident(g45,g46)
    c: Coincident(g46,g47)
    c: Coincident(g47,g44)
    c: Horizontal(g44)
    c: Horizontal(g46)
    c: Vertical(g45)
    c: Vertical(g47)
    c: Distance(g40) = 2
    c: Distance(g44) = 2
    c: Distance(g41) = 2
    c: Distance(g45) = 2
    c: DistanceY(g40,g37) = 1.2
    c: DistanceY(g44,g42) = 1.2
    c: DistanceX(g40,g-1) = 57.2
    c: DistanceX(g44,g-1) = 57.2
FEATURE [PartDesign::Pocket] Pocket004
  BaseFeature = -> LinearPattern002
  Length = 2.2
  Length2 = 100
  Profile = -> Sketch005
  Type = 0
FEATURE [PartDesign::LinearPattern] LinearPattern003
  BaseFeature = -> Pocket004
  Direction = -> Sketch005 [H_Axis]
  Length = 116.35
  Occurrences = 2
  Originals = -> [Pocket004]
FEATURE [Sketcher::SketchObject] Sketch006
  FullyConstrained = true
  MapMode = 5
  Placement = pos=(0,0,2.2) rot=(0,0,1;0rad)
  Support = -> [LinearPattern003]
  sketch-geometry (40):
    g0: LineSegment StartX=-62.4 StartY=15.4 StartZ=0 EndX=-60.4 EndY=15.4 EndZ=0
    g1: LineSegment StartX=-60.4 StartY=15.4 StartZ=0 EndX=-60.4 EndY=13.4 EndZ=0
    g2: LineSegment StartX=-60.4 StartY=13.4 StartZ=0 EndX=-62.4 EndY=13.4 EndZ=0
    g3: LineSegment StartX=-62.4 StartY=13.4 StartZ=0 EndX=-62.4 EndY=15.4 EndZ=0
    g4: LineSegment StartX=-62.4 StartY=12.2 StartZ=0 EndX=-60.4 EndY=12.2 EndZ=0
    g5: LineSegment StartX=-60.4 StartY=12.2 StartZ=0 EndX=-60.4 EndY=10.2 EndZ=0
    g6: LineSegment StartX=-60.4 StartY=10.2 StartZ=0 EndX=-62.4 EndY=10.2 EndZ=0
    g7: LineSegment StartX=-62.4 StartY=10.2 StartZ=0 EndX=-62.4 EndY=12.2 EndZ=0
    g8: LineSegment StartX=-62.4 StartY=9 StartZ=0 EndX=-60.4 EndY=9 EndZ=0
    g9: LineSegment StartX=-60.4 StartY=9 StartZ=0 EndX=-60.4 EndY=7 EndZ=0
    g10: LineSegment StartX=-60.4 StartY=7 StartZ=0 EndX=-62.4 EndY=7 EndZ=0
    g11: LineSegment StartX=-62.4 StartY=7 StartZ=0 EndX=-62.4 EndY=9 EndZ=0
    g12: LineSegment StartX=-62.4 StartY=5.8 StartZ=0 EndX=-60.4 EndY=5.8 EndZ=0
    g13: LineSegment StartX=-60.4 StartY=5.8 StartZ=0 EndX=-60.4 EndY=3.8 EndZ=0
    g14: LineSegment StartX=-60.4 StartY=3.8 StartZ=0 EndX=-62.4 EndY=3.8 EndZ=0
    g15: LineSegment StartX=-62.4 StartY=3.8 StartZ=0 EndX=-62.4 EndY=5.8 EndZ=0
    g16: LineSegment StartX=-62.4 StartY=2.6 StartZ=0 EndX=-60.4 EndY=2.6 EndZ=0
    g17: LineSegment StartX=-60.4 StartY=2.6 StartZ=0 EndX=-60.4 EndY=0.6 EndZ=0
    g18: LineSegment StartX=-60.4 StartY=0.6 StartZ=0 EndX=-62.4 EndY=0.6 EndZ=0
    g19: LineSegment StartX=-62.4 StartY=0.6 StartZ=0 EndX=-62.4 EndY=2.6 EndZ=0
    g20: LineSegment StartX=-62.4 StartY=-0.6 StartZ=0 EndX=-60.4 EndY=-0.6 EndZ=0
    g21: LineSegment StartX=-60.4 StartY=-0.6 StartZ=0 EndX=-60.4 EndY=-2.6 EndZ=0
    g22: LineSegment StartX=-60.4 StartY=-2.6 StartZ=0 EndX=-62.4 EndY=-2.6 EndZ=0
    g23: LineSegment StartX=-62.4 StartY=-2.6 StartZ=0 EndX=-62.4 EndY=-0.6 EndZ=0
    g24: LineSegment StartX=-62.4 StartY=-3.8 StartZ=0 EndX=-60.4 EndY=-3.8 EndZ=0
    g25: LineSegment StartX=-60.4 StartY=-3.8 StartZ=0 EndX=-60.4 EndY=-5.8 EndZ=0
    g26: LineSegment StartX=-60.4 StartY=-5.8 StartZ=0 EndX=-62.4 EndY=-5.8 EndZ=0
    g27: LineSegment StartX=-62.4 StartY=-5.8 StartZ=0 EndX=-62.4 EndY=-3.8 EndZ=0
    g28: LineSegment StartX=-60.4 StartY=-7 StartZ=0 EndX=-62.4 EndY=-7 EndZ=0
    g29: LineSegment StartX=-62.4 StartY=-7 StartZ=0 EndX=-62.4 EndY=-9 EndZ=0
    g30: LineSegment StartX=-62.4 StartY=-9 StartZ=0 EndX=-60.4 EndY=-9 EndZ=0
    g31: LineSegment StartX=-60.4 StartY=-9 StartZ=0 EndX=-60.4 EndY=-7 EndZ=0
    g32: LineSegment StartX=-62.4 StartY=-10.2 StartZ=0 EndX=-60.4 EndY=-10.2 EndZ=0
    g33: LineSegment StartX=-60.4 StartY=-10.2 StartZ=0 EndX=-60.4 EndY=-12.2 EndZ=0
    g34: LineSegment StartX=-60.4 StartY=-12.2 StartZ=0 EndX=-62.4 EndY=-12.2 EndZ=0
    g35: LineSegment StartX=-62.4 StartY=-12.2 StartZ=0 EndX=-62.4 EndY=-10.2 EndZ=0
    g36: LineSegment StartX=-62.4 StartY=-13.4 StartZ=0 EndX=-60.4 EndY=-13.4 EndZ=0
    g37: LineSegment StartX=-60.4 StartY=-13.4 StartZ=0 EndX=-60.4 EndY=-15.4 EndZ=0
    g38: LineSegment StartX=-60.4 StartY=-15.4 StartZ=0 EndX=-62.4 EndY=-15.4 EndZ=0
    g39: LineSegment StartX=-62.4 StartY=-15.4 StartZ=0 EndX=-62.4 EndY=-13.4 EndZ=0
  constraints (120):
    c: Coincident(g0,g1)
    c: Coincident(g1,g2)
    c: Coincident(g2,g3)
    c: Coincident(g3,g0)
    c: Horizontal(g0)
    c: Horizontal(g2)
    c: Vertical(g1)
    c: Vertical(g3)
    c: Coincident(g4,g5)
    c: Coincident(g5,g6)
    c: Coincident(g6,g7)
    c: Coincident(g7,g4)
    c: Horizontal(g4)
    c: Horizontal(g6)
    c: Vertical(g5)
    c: Vertical(g7)
    c: Coincident(g8,g9)
    c: Coincident(g9,g10)
    c: Coincident(g10,g11)
    c: Coincident(g11,g8)
    c: Horizontal(g8)
    c: Horizontal(g10)
    c: Vertical(g9)
    c: Vertical(g11)
    c: Coincident(g12,g13)
    c: Coincident(g13,g14)
    c: Coincident(g14,g15)
    c: Coincident(g15,g12)
    c: Horizontal(g12)
    c: Horizontal(g14)
    c: Vertical(g13)
    c: Vertical(g15)
    c: Coincident(g16,g17)
    c: Coincident(g17,g18)
    c: Coincident(g18,g19)
    c: Coincident(g19,g16)
    c: Horizontal(g16)
    c: Horizontal(g18)
    c: Vertical(g17)
    c: Vertical(g19)
    c: Distance(g16) = 2
    c: Distance(g17) = 2
    c: Distance(g13) = 2
    c: Distance(g14) = 2
    c: Distance(g10) = 2
    c: Distance(g9) = 2
    c: Distance(g6) = 2
    c: Distance(g5) = 2
    c: Distance(g2) = 2
    c: Distance(g1) = 2
    c: DistanceY(g-1,g17) = 0.6
    c: DistanceY(g16,g13) = 1.2
    c: DistanceY(g12,g9) = 1.2
    c: DistanceY(g8,g5) = 1.2
    c: DistanceY(g4,g1) = 1.2
    c: DistanceX(g17,g-1) = 60.4
    c: DistanceX(g13,g-1) = 60.4
    c: DistanceX(g9,g-1) = 60.4
    c: DistanceX(g5,g-1) = 60.4
    c: DistanceX(g1,g-1) = 60.4
    c: Coincident(g20,g21)
    c: Coincident(g21,g22)
    c: Coincident(g22,g23)
    c: Coincident(g23,g20)
    c: Horizontal(g20)
    c: Horizontal(g22)
    c: Vertical(g21)
    c: Vertical(g23)
    c: Coincident(g24,g25)
    c: Coincident(g25,g26)
    c: Coincident(g26,g27)
    c: Coincident(g27,g24)
    c: Horizontal(g24)
    c: Horizontal(g26)
    c: Vertical(g25)
    c: Vertical(g27)
    c: Coincident(g28,g29)
    c: Coincident(g29,g30)
    c: Coincident(g30,g31)
    c: Coincident(g31,g28)
    c: Horizontal(g28)
    c: Horizontal(g30)
    c: Vertical(g29)
    c: Vertical(g31)
    c: Distance(g20) = 2
    c: Distance(g21) = 2
    c: Distance(g24) = 2
    c: Distance(g25) = 2
    c: Distance(g28) = 2
    c: Distance(g29) = 2
    c: DistanceY(g20,g-1) = 0.6
    c: DistanceX(g20,g-1) = 60.4
    c: DistanceY(g24,g21) = 1.2
    c: DistanceX(g24,g21) = 0
    c: DistanceY(g28,g25) = 1.2
    c: DistanceX(g28,g25) = 2
    c: Coincident(g32,g33)
    c: Coincident(g33,g34)
    c: Coincident(g34,g35)
    c: Coincident(g35,g32)
    c: Horizontal(g32)
    c: Horizontal(g34)
    c: Vertical(g33)
    c: Vertical(g35)
    c: Coincident(g36,g37)
    c: Coincident(g37,g38)
    c: Coincident(g38,g39)
    c: Coincident(g39,g36)
    c: Horizontal(g36)
    c: Horizontal(g38)
    c: Vertical(g37)
    c: Vertical(g39)
    c: Distance(g32) = 2
    c: Distance(g33) = 2
    c: Distance(g36) = 2
    c: Distance(g37) = 2
    c: DistanceY(g32,g30) = 1.2
    c: DistanceY(g36,g33) = 1.2
    c: DistanceX(g32,g30) = 0
    c: DistanceX(g36,g33) = 0
FEATURE [PartDesign::Pocket] Pocket005
  BaseFeature = -> LinearPattern003
  Length = 2.2
  Length2 = 100
  Profile = -> Sketch006
  Type = 0
FEATURE [PartDesign::LinearPattern] LinearPattern004
  BaseFeature = -> Pocket005
  Direction = -> Sketch006 [H_Axis]
  Length = 122.9
  Occurrences = 2
  Originals = -> [Pocket005]
FEATURE [Sketcher::SketchObject] Sketch007
  FullyConstrained = true
  MapMode = 5
  Placement = pos=(0,0,2.2) rot=(0,0,1;0rad)
  Support = -> [LinearPattern004]
  sketch-geometry (32):
    g0: LineSegment StartX=-65.6 StartY=12.2 StartZ=0 EndX=-63.6 EndY=12.2 EndZ=0
    g1: LineSegment StartX=-63.6 StartY=12.2 StartZ=0 EndX=-63.6 EndY=10.2 EndZ=0
    g2: LineSegment StartX=-63.6 StartY=10.2 StartZ=0 EndX=-65.6 EndY=10.2 EndZ=0
    g3: LineSegment StartX=-65.6 StartY=10.2 StartZ=0 EndX=-65.6 EndY=12.2 EndZ=0
    g4: LineSegment StartX=-65.6 StartY=9 StartZ=0 EndX=-63.6 EndY=9 EndZ=0
    g5: LineSegment StartX=-63.6 StartY=9 StartZ=0 EndX=-63.6 EndY=7 EndZ=0
    g6: LineSegment StartX=-63.6 StartY=7 StartZ=0 EndX=-65.6 EndY=7 EndZ=0
    g7: LineSegment StartX=-65.6 StartY=7 StartZ=0 EndX=-65.6 EndY=9 EndZ=0
    g8: LineSegment StartX=-65.6 StartY=5.8 StartZ=0 EndX=-63.6 EndY=5.8 EndZ=0
    g9: LineSegment StartX=-63.6 StartY=5.8 StartZ=0 EndX=-63.6 EndY=3.8 EndZ=0
    g10: LineSegment StartX=-63.6 StartY=3.8 StartZ=0 EndX=-65.6 EndY=3.8 EndZ=0
    g11: LineSegment StartX=-65.6 StartY=3.8 StartZ=0 EndX=-65.6 EndY=5.8 EndZ=0
    g12: LineSegment StartX=-65.6 StartY=2.6 StartZ=0 EndX=-63.6 EndY=2.6 EndZ=0
    g13: LineSegment StartX=-63.6 StartY=2.6 StartZ=0 EndX=-63.6 EndY=0.6 EndZ=0
    g14: LineSegment StartX=-63.6 StartY=0.6 StartZ=0 EndX=-65.6 EndY=0.6 EndZ=0
    g15: LineSegment StartX=-65.6 StartY=0.6 StartZ=0 EndX=-65.6 EndY=2.6 EndZ=0
    g16: LineSegment StartX=-65.6 StartY=-0.6 StartZ=0 EndX=-63.6 EndY=-0.6 EndZ=0
    g17: LineSegment StartX=-63.6 StartY=-0.6 StartZ=0 EndX=-63.6 EndY=-2.6 EndZ=0
    g18: LineSegment StartX=-63.6 StartY=-2.6 StartZ=0 EndX=-65.6 EndY=-2.6 EndZ=0
    g19: LineSegment StartX=-65.6 StartY=-2.6 StartZ=0 EndX=-65.6 EndY=-0.6 EndZ=0
    g20: LineSegment StartX=-65.6 StartY=-3.8 StartZ=0 EndX=-63.6 EndY=-3.8 EndZ=0
    g21: LineSegment StartX=-63.6 StartY=-3.8 StartZ=0 EndX=-63.6 EndY=-5.8 EndZ=0
    g22: LineSegment StartX=-63.6 StartY=-5.8 StartZ=0 EndX=-65.6 EndY=-5.8 EndZ=0
    g23: LineSegment StartX=-65.6 StartY=-5.8 StartZ=0 EndX=-65.6 EndY=-3.8 EndZ=0
    g24: LineSegment StartX=-65.6 StartY=-10.2 StartZ=0 EndX=-63.6 EndY=-10.2 EndZ=0
    g25: LineSegment StartX=-63.6 StartY=-10.2 StartZ=0 EndX=-63.6 EndY=-12.2 EndZ=0
    g26: LineSegment StartX=-63.6 StartY=-12.2 StartZ=0 EndX=-65.6 EndY=-12.2 EndZ=0
    g27: LineSegment StartX=-65.6 StartY=-12.2 StartZ=0 EndX=-65.6 EndY=-10.2 EndZ=0
    g28: LineSegment StartX=-65.6 StartY=-7 StartZ=0 EndX=-63.6 EndY=-7 EndZ=0
    g29: LineSegment StartX=-63.6 StartY=-7 StartZ=0 EndX=-63.6 EndY=-9 EndZ=0
    g30: LineSegment StartX=-63.6 StartY=-9 StartZ=0 EndX=-65.6 EndY=-9 EndZ=0
    g31: LineSegment StartX=-65.6 StartY=-9 StartZ=0 EndX=-65.6 EndY=-7 EndZ=0
  constraints (96):
    c: Coincident(g0,g1)
    c: Coincident(g1,g2)
    c: Coincident(g2,g3)
    c: Coincident(g3,g0)
    c: Horizontal(g0)
    c: Horizontal(g2)
    c: Vertical(g1)
    c: Vertical(g3)
    c: Coincident(g4,g5)
    c: Coincident(g5,g6)
    c: Coincident(g6,g7)
    c: Coincident(g7,g4)
    c: Horizontal(g4)
    c: Horizontal(g6)
    c: Vertical(g5)
    c: Vertical(g7)
    c: Coincident(g8,g9)
    c: Coincident(g9,g10)
    c: Coincident(g10,g11)
    c: Coincident(g11,g8)
    c: Horizontal(g8)
    c: Horizontal(g10)
    c: Vertical(g9)
    c: Vertical(g11)
    c: Coincident(g12,g13)
    c: Coincident(g13,g14)
    c: Coincident(g14,g15)
    c: Coincident(g15,g12)
    c: Horizontal(g12)
    c: Horizontal(g14)
    c: Vertical(g13)
    c: Vertical(g15)
    c: Distance(g0) = 2
    c: Distance(g1) = 2
    c: Distance(g4) = 2
    c: Distance(g5) = 2
    c: Distance(g8) = 2
    c: Distance(g9) = 2
    c: Distance(g12) = 2
    c: Distance(g13) = 2
    c: DistanceX(g13,g-1) = 63.6
    c: DistanceX(g9,g12) = 0
    c: DistanceX(g5,g8) = 0
    c: DistanceX(g1,g4) = 0
    c: DistanceY(g12,g10) = 1.2
    c: DistanceY(g-1,g13) = 0.6
    c: DistanceY(g8,g5) = 1.2
    c: DistanceY(g4,g1) = 1.2
    c: Coincident(g16,g17)
    c: Coincident(g17,g18)
    c: Coincident(g18,g19)
    c: Coincident(g19,g16)
    c: Horizontal(g16)
    c: Horizontal(g18)
    c: Vertical(g17)
    c: Vertical(g19)
    c: Coincident(g20,g21)
    c: Coincident(g21,g22)
    c: Coincident(g22,g23)
    c: Coincident(g23,g20)
    c: Horizontal(g20)
    c: Horizontal(g22)
    c: Vertical(g21)
    c: Vertical(g23)
    c: Coincident(g24,g25)
    c: Coincident(g25,g26)
    c: Coincident(g26,g27)
    c: Coincident(g27,g24)
    c: Horizontal(g24)
    c: Horizontal(g26)
    c: Vertical(g25)
    c: Vertical(g27)
    c: Coincident(g28,g29)
    c: Coincident(g29,g30)
    c: Coincident(g30,g31)
    c: Coincident(g31,g28)
    c: Horizontal(g28)
    c: Horizontal(g30)
    c: Vertical(g29)
    c: Vertical(g31)
    c: Distance(g16) = 2
    c: Distance(g17) = 2
    c: DistanceY(g16,g-1) = 0.6
    c: DistanceX(g16,g13) = 0
    c: Distance(g20) = 2
    c: Distance(g21) = 2
    c: DistanceY(g20,g17) = 1.2
    c: DistanceX(g17,g20) = 0
    c: Distance(g28) = 2
    c: Distance(g29) = 2
    c: Distance(g24) = 2
    c: Distance(g25) = 2
    c: DistanceY(g28,g21) = 1.2
    c: DistanceX(g21,g28) = 0
    c: DistanceY(g24,g29) = 1.2
    c: DistanceX(g29,g24) = 0
FEATURE [PartDesign::Pocket] Pocket006
  BaseFeature = -> LinearPattern004
  Length = 2.2
  Length2 = 100
  Profile = -> Sketch007
  Type = 0
FEATURE [PartDesign::LinearPattern] LinearPattern005
  BaseFeature = -> Pocket006
  Direction = -> Sketch007 [H_Axis]
  Length = 129.4
  Occurrences = 2
  Originals = -> [Pocket006]
FEATURE [Sketcher::SketchObject] Sketch008
  FullyConstrained = true
  MapMode = 5
  Placement = pos=(0,0,2.2) rot=(0,0,1;0rad)
  Support = -> [LinearPattern005]
  sketch-geometry (24):
    g0: LineSegment StartX=-68.8 StartY=9 StartZ=0 EndX=-66.8 EndY=9 EndZ=0
    g1: LineSegment StartX=-66.8 StartY=9 StartZ=0 EndX=-66.8 EndY=7 EndZ=0
    g2: LineSegment StartX=-66.8 StartY=7 StartZ=0 EndX=-68.8 EndY=7 EndZ=0
    g3: LineSegment StartX=-68.8 StartY=7 StartZ=0 EndX=-68.8 EndY=9 EndZ=0
    g4: LineSegment StartX=-68.8 StartY=5.8 StartZ=0 EndX=-66.8 EndY=5.8 EndZ=0
    g5: LineSegment StartX=-66.8 StartY=5.8 StartZ=0 EndX=-66.8 EndY=3.8 EndZ=0
    g6: LineSegment StartX=-66.8 StartY=3.8 StartZ=0 EndX=-68.8 EndY=3.8 EndZ=0
    g7: LineSegment StartX=-68.8 StartY=3.8 StartZ=0 EndX=-68.8 EndY=5.8 EndZ=0
    g8: LineSegment StartX=-68.8 StartY=2.6 StartZ=0 EndX=-66.8 EndY=2.6 EndZ=0
    g9: LineSegment StartX=-66.8 StartY=2.6 StartZ=0 EndX=-66.8 EndY=0.6 EndZ=0
    g10: LineSegment StartX=-66.8 StartY=0.6 StartZ=0 EndX=-68.8 EndY=0.6 EndZ=0
    g11: LineSegment StartX=-68.8 StartY=0.6 StartZ=0 EndX=-68.8 EndY=2.6 EndZ=0
    g12: LineSegment StartX=-68.8 StartY=-0.6 StartZ=0 EndX=-66.8 EndY=-0.6 EndZ=0
    g13: LineSegment StartX=-66.8 StartY=-0.6 StartZ=0 EndX=-66.8 EndY=-2.6 EndZ=0
    g14: LineSegment StartX=-66.8 StartY=-2.6 StartZ=0 EndX=-68.8 EndY=-2.6 EndZ=0
    g15: LineSegment StartX=-68.8 StartY=-2.6 StartZ=0 EndX=-68.8 EndY=-0.6 EndZ=0
    g16: LineSegment StartX=-68.8 StartY=-7 StartZ=0 EndX=-66.8 EndY=-7 EndZ=0
    g17: LineSegment StartX=-66.8 StartY=-7 StartZ=0 EndX=-66.8 EndY=-9 EndZ=0
    g18: LineSegment StartX=-66.8 StartY=-9 StartZ=0 EndX=-68.8 EndY=-9 EndZ=0
    g19: LineSegment StartX=-68.8 StartY=-9 StartZ=0 EndX=-68.8 EndY=-7 EndZ=0
    g20: LineSegment StartX=-68.8 StartY=-3.8 StartZ=0 EndX=-66.8 EndY=-3.8 EndZ=0
    g21: LineSegment StartX=-66.8 StartY=-3.8 StartZ=0 EndX=-66.8 EndY=-5.8 EndZ=0
    g22: LineSegment StartX=-66.8 StartY=-5.8 StartZ=0 EndX=-68.8 EndY=-5.8 EndZ=0
    g23: LineSegment StartX=-68.8 StartY=-5.8 StartZ=0 EndX=-68.8 EndY=-3.8 EndZ=0
  constraints (72):
    c: Coincident(g0,g1)
    c: Coincident(g1,g2)
    c: Coincident(g2,g3)
    c: Coincident(g3,g0)
    c: Horizontal(g0)
    c: Horizontal(g2)
    c: Vertical(g1)
    c: Vertical(g3)
    c: Coincident(g4,g5)
    c: Coincident(g5,g6)
    c: Coincident(g6,g7)
    c: Coincident(g7,g4)
    c: Horizontal(g4)
    c: Horizontal(g6)
    c: Vertical(g5)
    c: Vertical(g7)
    c: Coincident(g8,g9)
    c: Coincident(g9,g10)
    c: Coincident(g10,g11)
    c: Coincident(g11,g8)
    c: Horizontal(g8)
    c: Horizontal(g10)
    c: Vertical(g9)
    c: Vertical(g11)
    c: Distance(g9) = 2
    c: Distance(g8) = 2
    c: DistanceX(g9,g-1) = 66.8
    c: DistanceY(g-1,g9) = 0.6
    c: Distance(g4) = 2
    c: Distance(g5) = 2
    c: Distance(g1) = 2
    c: Distance(g0) = 2
    c: DistanceY(g8,g5) = 1.2
    c: DistanceY(g4,g1) = 1.2
    c: DistanceX(g5,g8) = 0
    c: DistanceX(g1,g4) = 0
    c: Coincident(g12,g13)
    c: Coincident(g13,g14)
    c: Coincident(g14,g15)
    c: Coincident(g15,g12)
    c: Horizontal(g12)
    c: Horizontal(g14)
    c: Vertical(g13)
    c: Vertical(g15)
    c: Coincident(g16,g17)
    c: Coincident(g17,g18)
    c: Coincident(g18,g19)
    c: Coincident(g19,g16)
    c: Horizontal(g16)
    c: Horizontal(g18)
    c: Vertical(g17)
    c: Vertical(g19)
    c: Coincident(g20,g21)
    c: Coincident(g21,g22)
    c: Coincident(g22,g23)
    c: Coincident(g23,g20)
    c: Horizontal(g20)
    c: Horizontal(g22)
    c: Vertical(g21)
    c: Vertical(g23)
    c: Distance(g12) = 2
    c: Distance(g13) = 2
    c: Distance(g20) = 2
    c: Distance(g21) = 2
    c: Distance(g16) = 2
    c: Distance(g19) = 2
    c: DistanceY(g12,g-1) = 0.6
    c: DistanceY(g20,g13) = 1.2
    c: DistanceY(g16,g21) = 1.2
    c: DistanceX(g9,g12) = 0
    c: DistanceX(g20,g13) = 0
    c: DistanceX(g16,g21) = 0
FEATURE [PartDesign::Pocket] Pocket007
  BaseFeature = -> LinearPattern005
  Length = 2.2
  Length2 = 100
  Profile = -> Sketch008
  Type = 0
FEATURE [PartDesign::LinearPattern] LinearPattern006
  BaseFeature = -> Pocket007
  Direction = -> Sketch008 [H_Axis]
  Length = 135.85
  Occurrences = 2
  Originals = -> [Pocket007]
FEATURE [PartDesign::Chamfer] Chamfer
  Angle = 45
  Base = -> LinearPattern006 [Edge4404,Edge2902,Edge2209,Edge3711]
  BaseFeature = -> LinearPattern006
  ChamferType = 0
  FlipDirection = false
  Size = 2
  Size2 = 1
  SupportTransform = false
FEATURE [PartDesign::Body] Body
  Group = -> [Sketch,Pad,Sketch001,Pocket,Sketch002,Pocket001,LinearPattern,Sketch003,Pocket002,LinearPattern001,Sketch004,Pocket003,LinearPattern002,Sketch005,Pocket004,LinearPattern003,Sketch006,Pocket005,LinearPattern004,Sketch007,Pocket006,LinearPattern005,Sketch008,Pocket007,LinearPattern006,Chamfer]
  Origin = -> Origin
  Tip = -> Chamfer
